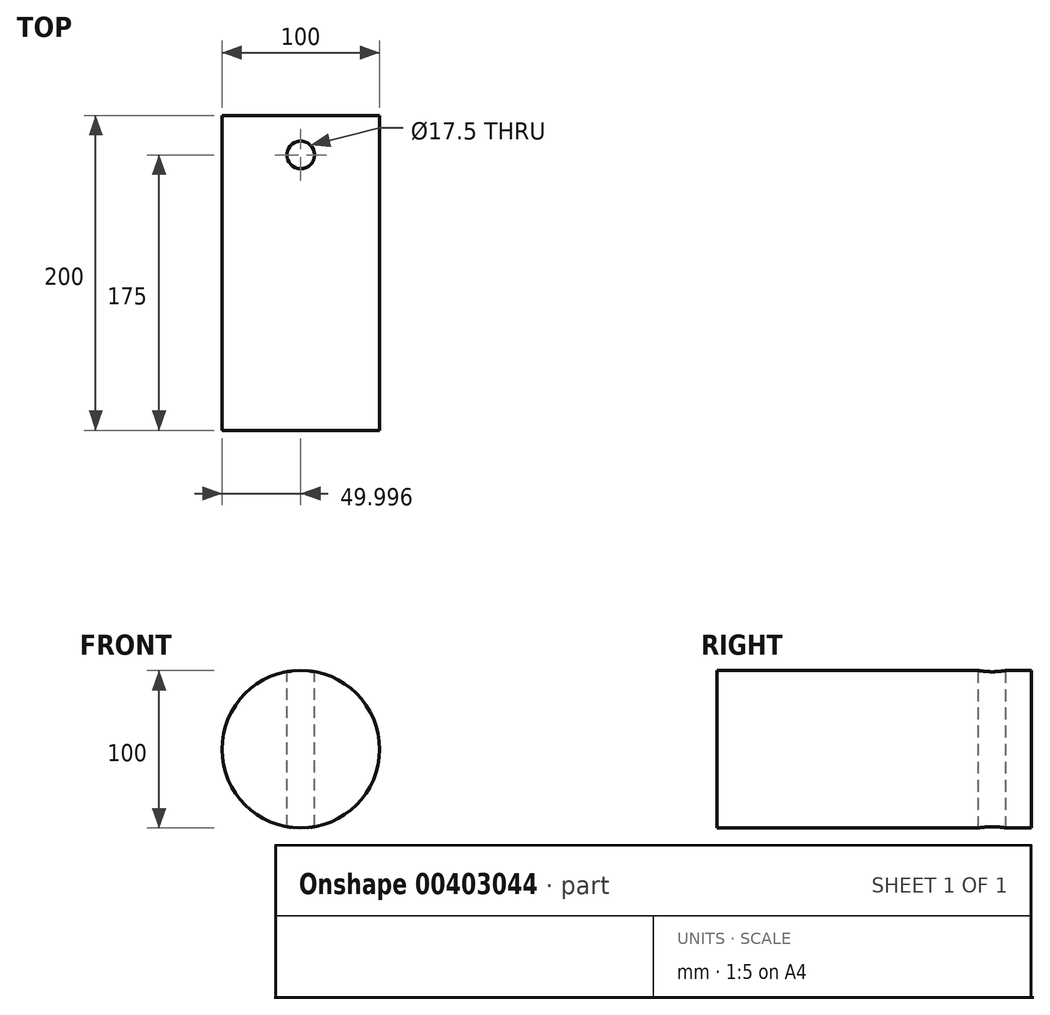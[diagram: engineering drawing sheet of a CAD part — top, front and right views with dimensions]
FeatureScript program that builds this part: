
annotation { "Feature Type Name" : "Feature", "Feature Type Description" : "" }
export const myFeature = defineFeature(function(context is Context, id is Id, definition is map)
    precondition{}
    {
        {
            var Q0;
            Q0=qCreatedBy(makeId("Front.planeOp"),FACE);
            var sketch = newSketch(context, id + "F0", { "sketchPlane" : qUnion([Q0])});
            skCircle(sketch, "E0", {"center": v(135.26, 19.52) * mm, "radius": 50 * mm});
            skSolve(sketch);
        }
        {
            var Q0;
            Q0 = qSketchRegion(id + "F0", true);
            extrude(context, id + "F1", {"entities" : qUnion([Q0]), "depth" : 200 * mm, "symmetric" : true});
        }
        {
            var Q0;
            Q0=makeQuery(id+"F1.opExtrude","CAP_FACE",FACE,{"disambiguationData":[OSD([sQuery(id+"F0.wireOp",EDGE,"E0")])],"isStart":true});
            cPlane(context, id + "F2", {"entities" : qUnion([Q0]), "cplaneType" : CPlaneType.OFFSET, "offset" : 25 * mm, "oppositeDirection" : true, "width" : 150 * mm, "height" : 150 * mm});
        }
        {
            var Q0;
            Q0=qCreatedBy(id+"F2.planeOp",FACE);
            var sketch = newSketch(context, id + "F3", { "sketchPlane" : qUnion([Q0])});
            skCircle(sketch, "E1.0", {"center": v(-135.26, 19.52) * mm, "radius": 50 * mm, "construction": true});
            skLineSegment(sketch, "E2", {"start": v(-135.26, 19.52) * mm, "end": v(-135.26, 69.52) * mm, "construction": true});
            skSolve(sketch);
        }
        {
            var Q0;
            Q0=sQuery(id+"F3.wireOp",EDGE,"E2");
            var Q1;
            Q1=sQuery(id+"F3.wireOp",VERTEX,"E2.end");
            cPlane(context, id + "F4", {"entities" : qUnion([Q0, Q1]), "cplaneType" : CPlaneType.LINE_POINT, "offset" : 25 * mm, "width" : 150 * mm, "height" : 150 * mm});
        }
        {
            var Q0;
            Q0=qCreatedBy(id+"F4.planeOp",FACE);
            var sketch = newSketch(context, id + "F5", { "sketchPlane" : qUnion([Q0])});
            skPoint(sketch, "E3.0", {"position": v(135.26, 75) * mm});
            skSolve(sketch);
        }
        {
            var Q0;
            Q0=sQuery(id+"F5.wireOp",VERTEX,"E3.0");
            var Q1;
            Q1=makeQuery(id+"F1.opExtrude","SWEPT_BODY",BODY,{"disambiguationData":[OSD([sQuery(id+"F0.wireOp",EDGE,"E0")])]});
            hole(context, id + "F6", {"style" : HoleStyle.SIMPLE, "endStyle" : HoleEndStyle.THROUGH, "standardTappedOrClearance" : lookupTablePath({ "standard" : "ISO", "engagement" : "75%", "pitch" : "2.5 mm", "size" : "M20", "type" : "Tapped" }), "standardBlindInLast" : lookupTablePath({ "standard" : "ISO", "engagement" : "75%", "pitch" : "2.5 mm", "size" : "M20", "type" : "Tapped" }), "holeDiameter" : 17.5 * mm, "showTappedDepth" : true, "tappedDepth" : 10 * mm, "tapClearance" : 0, "startFromSketch" : true, "locations" : qUnion([Q0]), "scope" : qUnion([Q1]), "majorDiameter" : 20 * mm});
        }
    });
